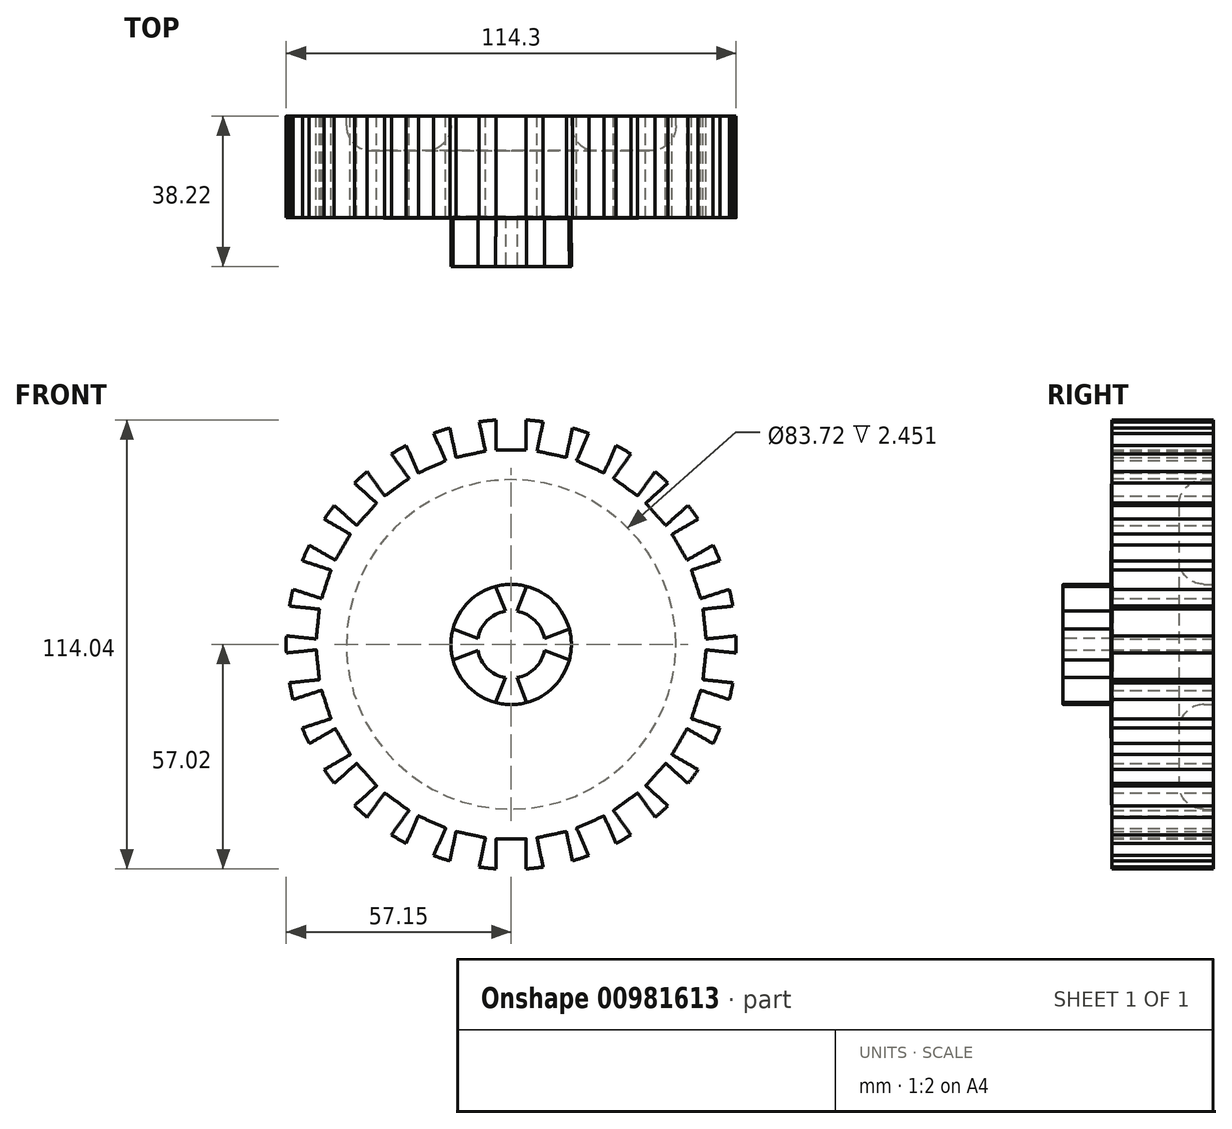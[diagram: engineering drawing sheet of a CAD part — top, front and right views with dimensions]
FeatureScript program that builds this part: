
annotation { "Feature Type Name" : "Feature", "Feature Type Description" : "" }
export const myFeature = defineFeature(function(context is Context, id is Id, definition is map)
    precondition{}
    {
        {
            var Q0;
            Q0=qCreatedBy(makeId("Right.planeOp"),FACE);
            var sketch = newSketch(context, id + "F0", { "sketchPlane" : qUnion([Q0])});
            skLineSegment(sketch, "E0.MirrorCS", {"start": v(38.22, 0) * mm, "end": v(12.13, 0) * mm});
            skLineSegment(sketch, "E1.MirrorCS", {"start": v(35.77, 15.29) * mm, "end": v(38.22, 15.29) * mm});
            skArc(sketch, "E2.MirrorCS", {"start": v(35.77, 15.29) * mm, "mid": v(31.28, 17.15) * mm, "end": v(29.42, 21.64) * mm});
            skLineSegment(sketch, "E3.MirrorCS", {"start": v(29.42, 35.51) * mm, "end": v(29.42, 21.64) * mm});
            skArc(sketch, "E4.MirrorCS", {"start": v(29.42, 35.51) * mm, "mid": v(31.28, 40) * mm, "end": v(35.77, 41.86) * mm});
            skLineSegment(sketch, "E5.MirrorCS", {"start": v(38.22, 41.86) * mm, "end": v(35.77, 41.86) * mm});
            skLineSegment(sketch, "E6.MirrorCS", {"start": v(38.22, 57.15) * mm, "end": v(38.22, 41.86) * mm});
            skLineSegment(sketch, "E7.MirrorCS", {"start": v(12.43, 57.15) * mm, "end": v(38.22, 57.15) * mm});
            skLineSegment(sketch, "E8.MirrorCS", {"start": v(38.22, 49.5) * mm, "end": v(12.39, 49.64) * mm});
            skLineSegment(sketch, "E9.MirrorCS", {"start": v(12.43, 57.15) * mm, "end": v(12.39, 49.64) * mm});
            skLineSegment(sketch, "E10", {"start": v(38.22, 15.29) * mm, "end": v(38.22, 0) * mm});
            skPoint(sketch, "E11.MirrorCS.end.orphan", {"position": v(-13.97, 0.27) * mm});
            skPoint(sketch, "E12.MirrorCS.end.orphan", {"position": v(12.13, 0) * mm});
            skPoint(sketch, "E13.MirrorCS.end.orphan", {"position": v(-13.8, 15.56) * mm});
            skPoint(sketch, "E13.MirrorCS.start.orphan", {"position": v(-11.36, 15.54) * mm});
            skLineSegment(sketch, "E14", {"start": v(12.13, 0) * mm, "end": v(0, 0) * mm});
            skLineSegment(sketch, "E15", {"start": v(0, 0) * mm, "end": v(0, 15.29) * mm});
            skLineSegment(sketch, "E16", {"start": v(0, 15.29) * mm, "end": v(12.13, 15.23) * mm});
            skLineSegment(sketch, "E17", {"start": v(12.39, 49.64) * mm, "end": v(12.13, 15.23) * mm});
            skSolve(sketch);
        }
        {
            var Q0;
            {var subQ0=sQuery(id+"F0.wireOp",EDGE,"E7.MirrorCS");Q0=makeQuery(id+"F0.imprint","IMPRINT",FACE,{"disambiguationData":[TD([[makeQuery(id+"F0.imprint","IMPRINT",EDGE,{"derivedFrom":subQ0}),-1.0]])]});}
            var Q1;
            {var subQ3=sQuery(id+"F0.wireOp",EDGE,"E0.MirrorCS");Q1=makeQuery(id+"F0.imprint","IMPRINT",FACE,{"disambiguationData":[TD([[makeQuery(id+"F0.imprint","IMPRINT",EDGE,{"derivedFrom":subQ3}),-1.0]])]});}
            var Q2;
            Q2=sQuery(id+"F0.wireOp",EDGE,"E0.MirrorCS");
            revolve(context, id + "F1", {"surfaceOperationType" : NewSurfaceOperationType.NEW, "entities" : qUnion([Q0, Q1]), "axis" : qUnion([Q2]), "revolveType" : RevolveType.FULL});
        }
        {
            var Q0;
            Q0=makeQuery(id+"F1.opRevolve","SWEPT_FACE",FACE,{"disambiguationData":[OSD([sQuery(id+"F0.wireOp",EDGE,"E6.MirrorCS")])]});
            var sketch = newSketch(context, id + "F2", { "sketchPlane" : qUnion([Q0])});
            skLineSegment(sketch, "E18", {"start": v(3.8, 57.02) * mm, "end": v(3.8, 49.4) * mm});
            skLineSegment(sketch, "E19", {"start": v(3.8, 49.4) * mm, "end": v(0, 49.4) * mm});
            skLineSegment(sketch, "E20.MirrorCS", {"start": v(-3.8, 57.02) * mm, "end": v(-3.8, 49.4) * mm});
            skLineSegment(sketch, "E21.MirrorCS", {"start": v(-3.8, 49.4) * mm, "end": v(0, 49.4) * mm});
            skSolve(sketch);
        }
        {
            var Q0;
            {var subQ1=sQuery(id+"F2.wireOp",EDGE,"E18");Q0=makeQuery(id+"F2.imprint","IMPRINT",FACE,{"disambiguationData":[TD([[makeQuery(id+"F2.imprint","IMPRINT",EDGE,{"derivedFrom":subQ1}),-1.0]])]});}
            extrude(context, id + "F3", {"entities" : qUnion([Q0]), "operationType" : NewBodyOperationType.REMOVE, "oppositeDirection" : true, "depth" : 27.94 * mm, "offsetDistance" : 25.4 * mm});
        }
        {
            var Q0;
            Q0=makeQuery(id+"F3.boolean.opBoolean","COPY",FACE,{"derivedFrom":makeQuery(id+"F3.opExtrude","SWEPT_FACE",FACE,{"disambiguationData":[OSD([sQuery(id+"F2.wireOp",EDGE,"E20.MirrorCS")])]})});
            var Q1;
            Q1=makeQuery(id+"F3.boolean.opBoolean","COPY",FACE,{"derivedFrom":makeQuery(id+"F3.opExtrude","CAP_FACE",FACE,{"disambiguationData":[OSD([sQuery(id+"F0.wireOp",EDGE,"E6.MirrorCS"),sQuery(id+"F0.wireOp",EDGE,"E7.MirrorCS"),sQuery(id+"F2.wireOp",EDGE,"E18"),sQuery(id+"F2.wireOp",EDGE,"E19"),sQuery(id+"F2.wireOp",EDGE,"E20.MirrorCS"),sQuery(id+"F2.wireOp",EDGE,"E21.MirrorCS")])],"isStart":false})});
            var Q2;
            Q2=makeQuery(id+"F3.boolean.opBoolean","COPY",FACE,{"derivedFrom":makeQuery(id+"F3.opExtrude","SWEPT_FACE",FACE,{"disambiguationData":[OSD([sQuery(id+"F2.wireOp",EDGE,"E18")])]})});
            var Q3;
            Q3=makeQuery(id+"F3.boolean.opBoolean","COPY",FACE,{"derivedFrom":makeQuery(id+"F3.opExtrude","SWEPT_FACE",FACE,{"disambiguationData":[OSD([sQuery(id+"F2.wireOp",EDGE,"E19"),sQuery(id+"F2.wireOp",EDGE,"E21.MirrorCS")])]})});
            var Q4;
            Q4=makeQuery(id+"F1.opRevolve","SWEPT_FACE",FACE,{"disambiguationData":[OSD([sQuery(id+"F0.wireOp",EDGE,"E7.MirrorCS")])]});
            circularPattern(context, id + "F4", {"patternType" : PatternType.FACE, "faces" : qUnion([Q0, Q1, Q2, Q3]), "axis" : qUnion([Q4]), "angle" : 360 * degree, "instanceCount" : 30, "equalSpace" : true});
        }
        {
            var Q0;
            Q0=makeQuery(id+"F1.opRevolve","SWEPT_FACE",FACE,{"disambiguationData":[OSD([sQuery(id+"F0.wireOp",EDGE,"E15")])]});
            var sketch = newSketch(context, id + "F5", { "sketchPlane" : qUnion([Q0])});
            skLineSegment(sketch, "E22", {"start": v(3.93, 14.78) * mm, "end": v(1.5, 8.45) * mm});
            skLineSegment(sketch, "E23", {"start": v(1.5, 8.45) * mm, "end": v(0, 8.45) * mm});
            skLineSegment(sketch, "E24.MirrorCS", {"start": v(-3.93, 14.78) * mm, "end": v(-1.5, 8.45) * mm});
            skLineSegment(sketch, "E25.MirrorCS", {"start": v(-1.5, 8.45) * mm, "end": v(0, 8.45) * mm});
            skCircle(sketch, "E26", {"center": v(0, 0) * mm, "radius": 8.58 * mm});
            skLineSegment(sketch, "E27.MirrorCS", {"start": v(-3.93, -14.78) * mm, "end": v(-1.5, -8.45) * mm});
            skLineSegment(sketch, "E28.MirrorCS", {"start": v(3.93, -14.78) * mm, "end": v(1.5, -8.45) * mm});
            skLineSegment(sketch, "E29.MirrorCS", {"start": v(-1.5, -8.45) * mm, "end": v(0, -8.45) * mm});
            skLineSegment(sketch, "E30.MirrorCS", {"start": v(1.5, -8.45) * mm, "end": v(0, -8.45) * mm});
            skLineSegment(sketch, "E31", {"start": v(8.45, 1.5) * mm, "end": v(14.78, 3.93) * mm});
            skLineSegment(sketch, "E32", {"start": v(8.45, 1.5) * mm, "end": v(8.71, 0) * mm});
            skLineSegment(sketch, "E33.MirrorCS", {"start": v(8.45, -1.5) * mm, "end": v(14.78, -3.93) * mm});
            skLineSegment(sketch, "E34.MirrorCS", {"start": v(8.45, -1.5) * mm, "end": v(8.71, 0) * mm});
            skLineSegment(sketch, "E35.MirrorCS", {"start": v(-8.45, 1.5) * mm, "end": v(-14.78, 3.93) * mm});
            skLineSegment(sketch, "E36.MirrorCS", {"start": v(-8.45, -1.5) * mm, "end": v(-14.78, -3.93) * mm});
            skLineSegment(sketch, "E37.MirrorCS", {"start": v(-8.45, -1.5) * mm, "end": v(-8.71, 0) * mm});
            skLineSegment(sketch, "E38.MirrorCS", {"start": v(-8.45, 1.5) * mm, "end": v(-8.71, 0) * mm});
            skCircle(sketch, "E39", {"center": v(0, 0) * mm, "radius": 4.13 * mm});
            skSolve(sketch);
        }
        {
            var Q0;
            {var subQ0=sQuery(id+"F5.wireOp",EDGE,"E24.MirrorCS");Q0=makeQuery(id+"F5.imprint","IMPRINT",FACE,{"disambiguationData":[TD([[makeQuery(id+"F5.imprint","IMPRINT",EDGE,{"derivedFrom":subQ0}),-1.0]])]});}
            var Q1;
            {var subQ0=sQuery(id+"F5.wireOp",EDGE,"E22");Q1=makeQuery(id+"F5.imprint","IMPRINT",FACE,{"disambiguationData":[TD([[makeQuery(id+"F5.imprint","IMPRINT",EDGE,{"derivedFrom":subQ0}),1.0]])]});}
            var Q2;
            {var subQ0=sQuery(id+"F5.wireOp",EDGE,"E27.MirrorCS");Q2=makeQuery(id+"F5.imprint","IMPRINT",FACE,{"disambiguationData":[TD([[makeQuery(id+"F5.imprint","IMPRINT",EDGE,{"derivedFrom":subQ0}),1.0]])]});}
            var Q3;
            {var subQ0=sQuery(id+"F5.wireOp",EDGE,"E28.MirrorCS");Q3=makeQuery(id+"F5.imprint","IMPRINT",FACE,{"disambiguationData":[TD([[makeQuery(id+"F5.imprint","IMPRINT",EDGE,{"derivedFrom":subQ0}),-1.0]])]});}
            extrude(context, id + "F6", {"entities" : qUnion([Q0, Q1, Q2, Q3]), "operationType" : NewBodyOperationType.REMOVE, "oppositeDirection" : true, "depth" : 12.7 * mm, "offsetDistance" : 25.4 * mm});
        }
    });
